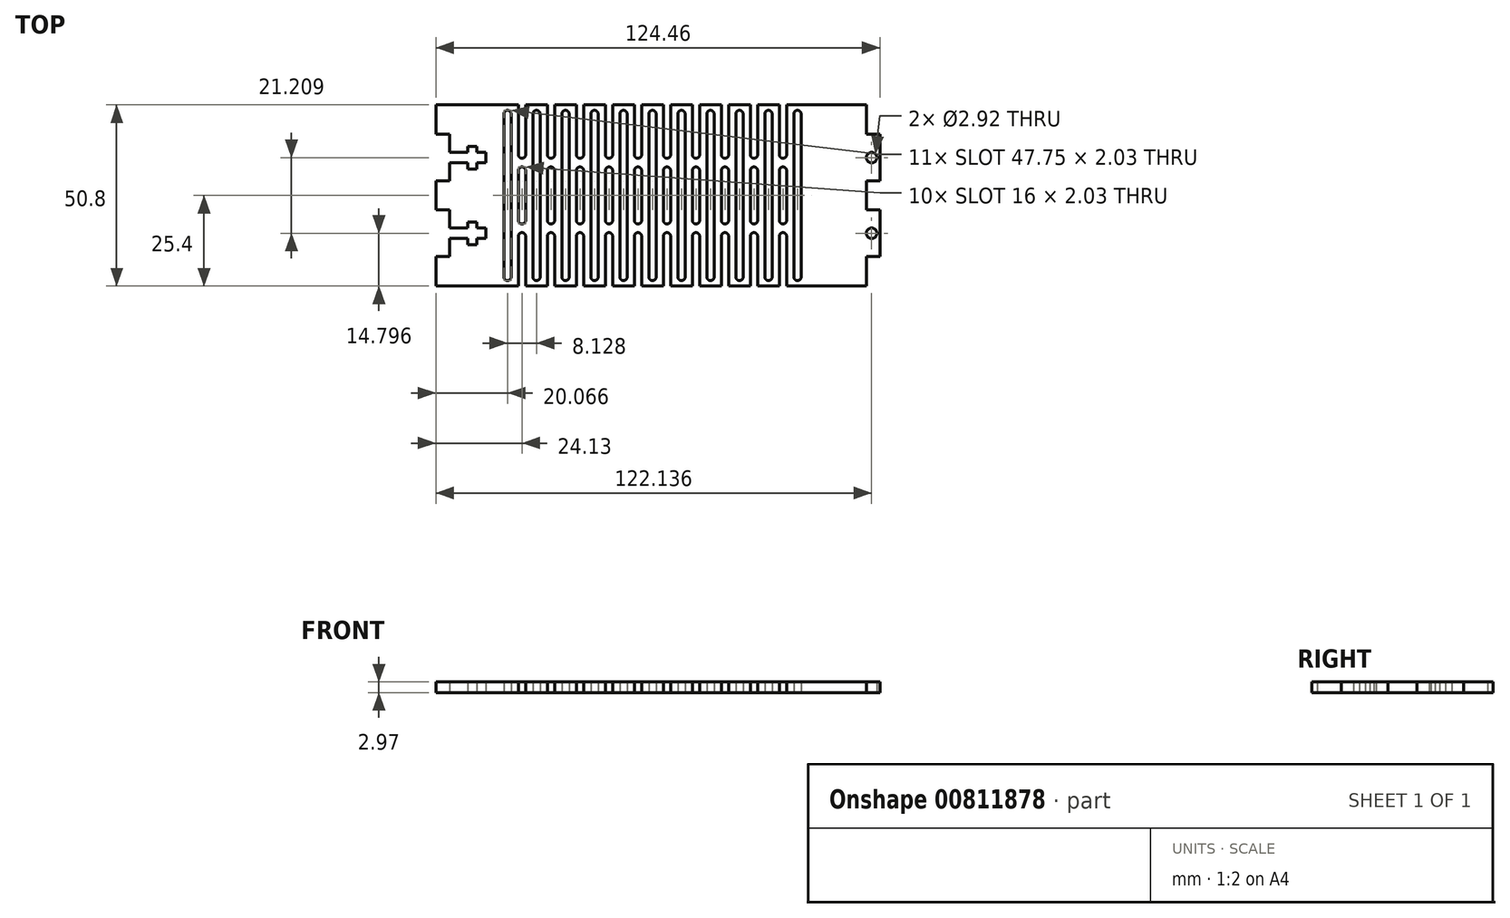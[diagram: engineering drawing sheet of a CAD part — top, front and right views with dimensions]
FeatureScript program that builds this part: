
annotation { "Feature Type Name" : "Feature", "Feature Type Description" : "" }
export const myFeature = defineFeature(function(context is Context, id is Id, definition is map)
    precondition{}
    {
        {
            var Q0;
            Q0=qCreatedBy(makeId("Top.planeOp"),FACE);
            var sketch = newSketch(context, id + "F0", { "sketchPlane" : qUnion([Q0])});
            skLineSegment(sketch, "E0", {"start": v(0, 8.26) * mm, "end": v(3.81, 8.26) * mm});
            skLineSegment(sketch, "E1", {"start": v(3.81, 8.26) * mm, "end": v(3.81, 13.34) * mm});
            skLineSegment(sketch, "E2", {"start": v(3.81, 13.34) * mm, "end": v(8.9, 13.34) * mm});
            skLineSegment(sketch, "E3", {"start": v(8.9, 13.34) * mm, "end": v(8.9, 11.6) * mm});
            skLineSegment(sketch, "E4", {"start": v(8.9, 11.6) * mm, "end": v(11.43, 11.6) * mm});
            skLineSegment(sketch, "E5", {"start": v(11.43, 11.6) * mm, "end": v(11.43, 13.34) * mm});
            skLineSegment(sketch, "E6", {"start": v(11.43, 13.34) * mm, "end": v(13.97, 13.34) * mm});
            skLineSegment(sketch, "E7", {"start": v(13.97, 13.34) * mm, "end": v(13.97, 16.26) * mm});
            skLineSegment(sketch, "E8", {"start": v(13.97, 16.26) * mm, "end": v(11.43, 16.26) * mm});
            skLineSegment(sketch, "E9", {"start": v(11.43, 16.26) * mm, "end": v(11.43, 17.98) * mm});
            skLineSegment(sketch, "E10", {"start": v(11.43, 17.98) * mm, "end": v(8.9, 17.98) * mm});
            skLineSegment(sketch, "E11", {"start": v(8.9, 17.98) * mm, "end": v(8.9, 16.26) * mm});
            skLineSegment(sketch, "E12", {"start": v(8.9, 16.26) * mm, "end": v(3.81, 16.26) * mm});
            skLineSegment(sketch, "E13", {"start": v(3.81, 16.26) * mm, "end": v(3.81, 21.34) * mm});
            skLineSegment(sketch, "E14", {"start": v(3.81, 21.34) * mm, "end": v(0, 21.34) * mm});
            skLineSegment(sketch, "E15", {"start": v(0, 0) * mm, "end": v(0, 8.26) * mm});
            skLineSegment(sketch, "E16", {"start": v(0, 50.8) * mm, "end": v(0, 42.55) * mm});
            skLineSegment(sketch, "E17", {"start": v(0, 42.55) * mm, "end": v(3.81, 42.55) * mm});
            skLineSegment(sketch, "E18", {"start": v(3.81, 42.54) * mm, "end": v(3.81, 37.46) * mm});
            skLineSegment(sketch, "E19", {"start": v(3.81, 37.46) * mm, "end": v(8.89, 37.46) * mm});
            skLineSegment(sketch, "E20", {"start": v(8.89, 37.46) * mm, "end": v(8.89, 39.2) * mm});
            skLineSegment(sketch, "E21", {"start": v(8.89, 39.2) * mm, "end": v(11.43, 39.2) * mm});
            skLineSegment(sketch, "E22", {"start": v(11.43, 39.2) * mm, "end": v(11.43, 37.46) * mm});
            skLineSegment(sketch, "E23", {"start": v(11.43, 37.46) * mm, "end": v(13.97, 37.46) * mm});
            skLineSegment(sketch, "E24", {"start": v(13.97, 37.46) * mm, "end": v(13.97, 34.54) * mm});
            skLineSegment(sketch, "E25", {"start": v(13.97, 34.54) * mm, "end": v(11.43, 34.54) * mm});
            skLineSegment(sketch, "E26", {"start": v(11.43, 34.54) * mm, "end": v(11.43, 32.82) * mm});
            skLineSegment(sketch, "E27", {"start": v(11.43, 32.82) * mm, "end": v(8.89, 32.82) * mm});
            skLineSegment(sketch, "E28", {"start": v(8.89, 32.82) * mm, "end": v(8.89, 34.54) * mm});
            skLineSegment(sketch, "E29", {"start": v(8.89, 34.54) * mm, "end": v(3.81, 34.54) * mm});
            skLineSegment(sketch, "E30", {"start": v(3.81, 34.54) * mm, "end": v(3.81, 29.46) * mm});
            skLineSegment(sketch, "E31", {"start": v(3.81, 29.46) * mm, "end": v(0, 29.46) * mm});
            skLineSegment(sketch, "E32", {"start": v(0, 29.46) * mm, "end": v(0, 21.34) * mm});
            skLineSegment(sketch, "E33", {"start": v(120.65, 0) * mm, "end": v(120.65, 8.26) * mm});
            skLineSegment(sketch, "E34", {"start": v(120.65, 8.26) * mm, "end": v(124.46, 8.26) * mm});
            skLineSegment(sketch, "E35", {"start": v(124.46, 8.26) * mm, "end": v(124.46, 21.34) * mm});
            skLineSegment(sketch, "E36", {"start": v(124.46, 21.34) * mm, "end": v(120.65, 21.34) * mm});
            skLineSegment(sketch, "E37", {"start": v(120.65, 21.34) * mm, "end": v(120.65, 29.46) * mm});
            skLineSegment(sketch, "E38", {"start": v(120.65, 29.46) * mm, "end": v(124.46, 29.46) * mm});
            skLineSegment(sketch, "E39", {"start": v(124.46, 29.46) * mm, "end": v(124.46, 42.55) * mm});
            skLineSegment(sketch, "E40", {"start": v(124.46, 42.55) * mm, "end": v(120.65, 42.55) * mm});
            skLineSegment(sketch, "E41", {"start": v(120.65, 42.55) * mm, "end": v(120.65, 50.8) * mm});
            skCircle(sketch, "E42", {"center": v(122.14, 14.8) * mm, "radius": 1.46 * mm});
            skCircle(sketch, "E43", {"center": v(122.14, 36) * mm, "radius": 1.46 * mm});
            skLineSegment(sketch, "E44", {"start": v(19.05, 2.54) * mm, "end": v(19.05, 48.26) * mm});
            skLineSegment(sketch, "E45", {"start": v(21.08, 2.54) * mm, "end": v(21.08, 48.26) * mm});
            skArc(sketch, "E46", {"start": v(19.05, 48.26) * mm, "mid": v(20.07, 49.28) * mm, "end": v(21.08, 48.26) * mm});
            skArc(sketch, "E47", {"start": v(19.05, 2.54) * mm, "mid": v(20.07, 1.52) * mm, "end": v(21.08, 2.54) * mm});
            skLineSegment(sketch, "E48", {"start": v(23.11, 50.8) * mm, "end": v(23.11, 36.83) * mm});
            skLineSegment(sketch, "E49", {"start": v(0, 50.8) * mm, "end": v(23.11, 50.8) * mm});
            skLineSegment(sketch, "E50", {"start": v(0, 0) * mm, "end": v(23.11, 0) * mm});
            skLineSegment(sketch, "E51", {"start": v(25.15, 50.8) * mm, "end": v(25.15, 36.83) * mm});
            skArc(sketch, "E52", {"start": v(23.11, 36.83) * mm, "mid": v(24.13, 35.81) * mm, "end": v(25.15, 36.83) * mm});
            skLineSegment(sketch, "E53", {"start": v(23.11, 32.39) * mm, "end": v(23.11, 18.42) * mm});
            skLineSegment(sketch, "E54", {"start": v(25.15, 32.39) * mm, "end": v(25.15, 18.42) * mm});
            skLineSegment(sketch, "E55", {"start": v(23.11, 0) * mm, "end": v(23.11, 13.97) * mm});
            skLineSegment(sketch, "E56", {"start": v(25.15, 13.97) * mm, "end": v(25.15, 0) * mm});
            skArc(sketch, "E57", {"start": v(23.11, 32.39) * mm, "mid": v(24.13, 33.4) * mm, "end": v(25.15, 32.39) * mm});
            skArc(sketch, "E58", {"start": v(23.11, 18.42) * mm, "mid": v(24.13, 17.4) * mm, "end": v(25.15, 18.42) * mm});
            skArc(sketch, "E59", {"start": v(25.15, 13.97) * mm, "mid": v(24.13, 14.99) * mm, "end": v(23.11, 13.97) * mm});
            skLineSegment(sketch, "E60", {"start": v(25.15, 50.8) * mm, "end": v(31.24, 50.8) * mm});
            skLineSegment(sketch, "E61", {"start": v(25.15, 0) * mm, "end": v(31.24, 0) * mm});
            skLineSegment(sketch, "E62", {"start": v(27.18, 2.54) * mm, "end": v(27.18, 48.26) * mm});
            skLineSegment(sketch, "E63", {"start": v(29.2, 2.54) * mm, "end": v(29.2, 48.26) * mm});
            skArc(sketch, "E64", {"start": v(27.18, 48.26) * mm, "mid": v(28.2, 49.28) * mm, "end": v(29.2, 48.26) * mm});
            skArc(sketch, "E65", {"start": v(27.18, 2.54) * mm, "mid": v(28.2, 1.52) * mm, "end": v(29.2, 2.54) * mm});
            skLineSegment(sketch, "E66", {"start": v(31.24, 50.8) * mm, "end": v(31.24, 36.83) * mm});
            skLineSegment(sketch, "E67", {"start": v(33.27, 50.8) * mm, "end": v(33.27, 36.83) * mm});
            skArc(sketch, "E68", {"start": v(31.24, 36.83) * mm, "mid": v(32.26, 35.81) * mm, "end": v(33.27, 36.83) * mm});
            skLineSegment(sketch, "E69", {"start": v(31.24, 32.39) * mm, "end": v(31.24, 18.42) * mm});
            skLineSegment(sketch, "E70", {"start": v(33.27, 32.39) * mm, "end": v(33.27, 18.42) * mm});
            skLineSegment(sketch, "E71", {"start": v(31.24, 0) * mm, "end": v(31.24, 13.97) * mm});
            skLineSegment(sketch, "E72", {"start": v(33.27, 13.97) * mm, "end": v(33.27, 0) * mm});
            skArc(sketch, "E73", {"start": v(31.24, 32.39) * mm, "mid": v(32.26, 33.4) * mm, "end": v(33.27, 32.39) * mm});
            skArc(sketch, "E74", {"start": v(31.24, 18.42) * mm, "mid": v(32.26, 17.4) * mm, "end": v(33.27, 18.42) * mm});
            skArc(sketch, "E75", {"start": v(33.27, 13.97) * mm, "mid": v(32.26, 14.99) * mm, "end": v(31.24, 13.97) * mm});
            skLineSegment(sketch, "E76", {"start": v(33.27, 0) * mm, "end": v(39.37, 0) * mm});
            skLineSegment(sketch, "E77", {"start": v(35.3, 2.54) * mm, "end": v(35.3, 48.26) * mm});
            skLineSegment(sketch, "E78", {"start": v(37.34, 2.54) * mm, "end": v(37.34, 48.26) * mm});
            skArc(sketch, "E79", {"start": v(35.3, 48.26) * mm, "mid": v(36.32, 49.28) * mm, "end": v(37.34, 48.26) * mm});
            skArc(sketch, "E80", {"start": v(35.3, 2.54) * mm, "mid": v(36.32, 1.52) * mm, "end": v(37.34, 2.54) * mm});
            skLineSegment(sketch, "E81", {"start": v(39.37, 50.8) * mm, "end": v(39.37, 36.83) * mm});
            skLineSegment(sketch, "E82", {"start": v(41.4, 50.8) * mm, "end": v(41.4, 36.83) * mm});
            skArc(sketch, "E83", {"start": v(39.37, 36.83) * mm, "mid": v(40.39, 35.81) * mm, "end": v(41.4, 36.83) * mm});
            skLineSegment(sketch, "E84", {"start": v(39.37, 32.39) * mm, "end": v(39.37, 18.42) * mm});
            skLineSegment(sketch, "E85", {"start": v(41.4, 32.39) * mm, "end": v(41.4, 18.42) * mm});
            skLineSegment(sketch, "E86", {"start": v(39.37, 0) * mm, "end": v(39.37, 13.97) * mm});
            skLineSegment(sketch, "E87", {"start": v(41.4, 13.97) * mm, "end": v(41.4, 0) * mm});
            skArc(sketch, "E88", {"start": v(39.37, 32.39) * mm, "mid": v(40.39, 33.4) * mm, "end": v(41.4, 32.39) * mm});
            skArc(sketch, "E89", {"start": v(39.37, 18.42) * mm, "mid": v(40.39, 17.4) * mm, "end": v(41.4, 18.42) * mm});
            skArc(sketch, "E90", {"start": v(41.4, 13.97) * mm, "mid": v(40.39, 14.99) * mm, "end": v(39.37, 13.97) * mm});
            skLineSegment(sketch, "E91", {"start": v(41.4, 50.8) * mm, "end": v(47.5, 50.8) * mm});
            skLineSegment(sketch, "E92", {"start": v(43.43, 2.54) * mm, "end": v(43.43, 48.26) * mm});
            skLineSegment(sketch, "E93", {"start": v(45.47, 2.54) * mm, "end": v(45.47, 48.26) * mm});
            skArc(sketch, "E94", {"start": v(43.43, 48.26) * mm, "mid": v(44.45, 49.28) * mm, "end": v(45.47, 48.26) * mm});
            skArc(sketch, "E95", {"start": v(43.43, 2.54) * mm, "mid": v(44.45, 1.52) * mm, "end": v(45.47, 2.54) * mm});
            skLineSegment(sketch, "E96", {"start": v(47.5, 50.8) * mm, "end": v(47.5, 36.83) * mm});
            skLineSegment(sketch, "E97", {"start": v(49.53, 50.8) * mm, "end": v(49.53, 36.83) * mm});
            skArc(sketch, "E98", {"start": v(47.5, 36.83) * mm, "mid": v(48.51, 35.81) * mm, "end": v(49.53, 36.83) * mm});
            skLineSegment(sketch, "E99", {"start": v(47.5, 32.39) * mm, "end": v(47.5, 18.42) * mm});
            skLineSegment(sketch, "E100", {"start": v(49.53, 32.39) * mm, "end": v(49.53, 18.42) * mm});
            skLineSegment(sketch, "E101", {"start": v(47.5, 0) * mm, "end": v(47.5, 13.97) * mm});
            skLineSegment(sketch, "E102", {"start": v(49.53, 13.97) * mm, "end": v(49.53, 0) * mm});
            skArc(sketch, "E103", {"start": v(47.5, 32.39) * mm, "mid": v(48.51, 33.4) * mm, "end": v(49.53, 32.39) * mm});
            skArc(sketch, "E104", {"start": v(47.5, 18.42) * mm, "mid": v(48.51, 17.4) * mm, "end": v(49.53, 18.42) * mm});
            skArc(sketch, "E105", {"start": v(49.53, 13.97) * mm, "mid": v(48.51, 14.99) * mm, "end": v(47.5, 13.97) * mm});
            skLineSegment(sketch, "E106", {"start": v(49.53, 50.8) * mm, "end": v(55.63, 50.8) * mm});
            skLineSegment(sketch, "E107", {"start": v(49.53, 0) * mm, "end": v(55.63, 0) * mm});
            skLineSegment(sketch, "E108", {"start": v(33.27, 50.8) * mm, "end": v(39.37, 50.8) * mm});
            skLineSegment(sketch, "E109", {"start": v(41.4, 0) * mm, "end": v(47.5, 0) * mm});
            skLineSegment(sketch, "E110", {"start": v(51.56, 2.54) * mm, "end": v(51.56, 48.26) * mm});
            skLineSegment(sketch, "E111", {"start": v(53.6, 2.54) * mm, "end": v(53.6, 48.26) * mm});
            skArc(sketch, "E112", {"start": v(51.56, 48.26) * mm, "mid": v(52.58, 49.28) * mm, "end": v(53.6, 48.26) * mm});
            skArc(sketch, "E113", {"start": v(51.56, 2.54) * mm, "mid": v(52.58, 1.52) * mm, "end": v(53.6, 2.54) * mm});
            skLineSegment(sketch, "E114", {"start": v(55.63, 50.8) * mm, "end": v(55.63, 36.83) * mm});
            skLineSegment(sketch, "E115", {"start": v(57.66, 50.8) * mm, "end": v(57.66, 36.83) * mm});
            skArc(sketch, "E116", {"start": v(55.63, 36.83) * mm, "mid": v(56.64, 35.81) * mm, "end": v(57.66, 36.83) * mm});
            skLineSegment(sketch, "E117", {"start": v(55.63, 32.39) * mm, "end": v(55.63, 18.42) * mm});
            skLineSegment(sketch, "E118", {"start": v(57.66, 32.39) * mm, "end": v(57.66, 18.42) * mm});
            skLineSegment(sketch, "E119", {"start": v(55.63, 0) * mm, "end": v(55.63, 13.97) * mm});
            skLineSegment(sketch, "E120", {"start": v(57.66, 13.97) * mm, "end": v(57.66, 0) * mm});
            skArc(sketch, "E121", {"start": v(55.63, 32.39) * mm, "mid": v(56.64, 33.4) * mm, "end": v(57.66, 32.39) * mm});
            skArc(sketch, "E122", {"start": v(55.63, 18.42) * mm, "mid": v(56.64, 17.4) * mm, "end": v(57.66, 18.42) * mm});
            skArc(sketch, "E123", {"start": v(57.66, 13.97) * mm, "mid": v(56.64, 14.99) * mm, "end": v(55.63, 13.97) * mm});
            skLineSegment(sketch, "E124", {"start": v(57.66, 50.8) * mm, "end": v(63.75, 50.8) * mm});
            skLineSegment(sketch, "E125", {"start": v(57.66, 0) * mm, "end": v(63.75, 0) * mm});
            skLineSegment(sketch, "E126", {"start": v(59.7, 2.54) * mm, "end": v(59.7, 48.26) * mm});
            skLineSegment(sketch, "E127", {"start": v(61.72, 2.54) * mm, "end": v(61.72, 48.26) * mm});
            skArc(sketch, "E128", {"start": v(59.69, 48.26) * mm, "mid": v(60.7, 49.28) * mm, "end": v(61.72, 48.26) * mm});
            skArc(sketch, "E129", {"start": v(59.69, 2.54) * mm, "mid": v(60.7, 1.52) * mm, "end": v(61.72, 2.54) * mm});
            skLineSegment(sketch, "E130", {"start": v(63.75, 50.8) * mm, "end": v(63.75, 36.83) * mm});
            skLineSegment(sketch, "E131", {"start": v(65.79, 50.8) * mm, "end": v(65.79, 36.83) * mm});
            skArc(sketch, "E132", {"start": v(63.75, 36.83) * mm, "mid": v(64.77, 35.81) * mm, "end": v(65.79, 36.83) * mm});
            skLineSegment(sketch, "E133", {"start": v(63.75, 32.39) * mm, "end": v(63.75, 18.42) * mm});
            skLineSegment(sketch, "E134", {"start": v(65.79, 32.39) * mm, "end": v(65.79, 18.42) * mm});
            skLineSegment(sketch, "E135", {"start": v(63.75, 0) * mm, "end": v(63.75, 13.97) * mm});
            skLineSegment(sketch, "E136", {"start": v(65.79, 13.97) * mm, "end": v(65.79, 0) * mm});
            skArc(sketch, "E137", {"start": v(63.75, 32.39) * mm, "mid": v(64.77, 33.4) * mm, "end": v(65.79, 32.39) * mm});
            skArc(sketch, "E138", {"start": v(63.75, 18.42) * mm, "mid": v(64.77, 17.4) * mm, "end": v(65.79, 18.42) * mm});
            skArc(sketch, "E139", {"start": v(65.79, 13.97) * mm, "mid": v(64.77, 14.99) * mm, "end": v(63.75, 13.97) * mm});
            skLineSegment(sketch, "E140", {"start": v(65.79, 0) * mm, "end": v(71.88, 0) * mm});
            skLineSegment(sketch, "E141", {"start": v(67.82, 2.54) * mm, "end": v(67.82, 48.26) * mm});
            skLineSegment(sketch, "E142", {"start": v(69.85, 2.54) * mm, "end": v(69.85, 48.26) * mm});
            skArc(sketch, "E143", {"start": v(67.82, 48.26) * mm, "mid": v(68.83, 49.28) * mm, "end": v(69.85, 48.26) * mm});
            skArc(sketch, "E144", {"start": v(67.82, 2.54) * mm, "mid": v(68.83, 1.52) * mm, "end": v(69.85, 2.54) * mm});
            skLineSegment(sketch, "E145", {"start": v(71.88, 50.8) * mm, "end": v(71.88, 36.83) * mm});
            skLineSegment(sketch, "E146", {"start": v(73.91, 50.8) * mm, "end": v(73.91, 36.83) * mm});
            skArc(sketch, "E147", {"start": v(71.88, 36.83) * mm, "mid": v(72.9, 35.81) * mm, "end": v(73.91, 36.83) * mm});
            skLineSegment(sketch, "E148", {"start": v(71.88, 32.39) * mm, "end": v(71.88, 18.42) * mm});
            skLineSegment(sketch, "E149", {"start": v(73.91, 32.39) * mm, "end": v(73.91, 18.42) * mm});
            skLineSegment(sketch, "E150", {"start": v(71.88, 0) * mm, "end": v(71.88, 13.97) * mm});
            skLineSegment(sketch, "E151", {"start": v(73.91, 13.97) * mm, "end": v(73.91, 0) * mm});
            skArc(sketch, "E152", {"start": v(71.88, 32.39) * mm, "mid": v(72.9, 33.4) * mm, "end": v(73.91, 32.39) * mm});
            skArc(sketch, "E153", {"start": v(71.88, 18.42) * mm, "mid": v(72.9, 17.4) * mm, "end": v(73.91, 18.42) * mm});
            skArc(sketch, "E154", {"start": v(73.91, 13.97) * mm, "mid": v(72.9, 14.99) * mm, "end": v(71.88, 13.97) * mm});
            skLineSegment(sketch, "E155", {"start": v(73.91, 50.8) * mm, "end": v(80.01, 50.8) * mm});
            skLineSegment(sketch, "E156", {"start": v(75.95, 2.54) * mm, "end": v(75.95, 48.26) * mm});
            skLineSegment(sketch, "E157", {"start": v(77.98, 2.54) * mm, "end": v(77.98, 48.26) * mm});
            skArc(sketch, "E158", {"start": v(75.95, 48.26) * mm, "mid": v(76.96, 49.28) * mm, "end": v(77.98, 48.26) * mm});
            skArc(sketch, "E159", {"start": v(75.95, 2.54) * mm, "mid": v(76.96, 1.52) * mm, "end": v(77.98, 2.54) * mm});
            skLineSegment(sketch, "E160", {"start": v(80.01, 50.8) * mm, "end": v(80.01, 36.83) * mm});
            skLineSegment(sketch, "E161", {"start": v(82.04, 50.8) * mm, "end": v(82.04, 36.83) * mm});
            skArc(sketch, "E162", {"start": v(80.01, 36.83) * mm, "mid": v(81.03, 35.81) * mm, "end": v(82.04, 36.83) * mm});
            skLineSegment(sketch, "E163", {"start": v(80.01, 32.39) * mm, "end": v(80.01, 18.42) * mm});
            skLineSegment(sketch, "E164", {"start": v(82.04, 32.39) * mm, "end": v(82.04, 18.42) * mm});
            skLineSegment(sketch, "E165", {"start": v(80.01, 0) * mm, "end": v(80.01, 13.97) * mm});
            skLineSegment(sketch, "E166", {"start": v(82.04, 13.97) * mm, "end": v(82.04, 0) * mm});
            skArc(sketch, "E167", {"start": v(80.01, 32.39) * mm, "mid": v(81.03, 33.4) * mm, "end": v(82.04, 32.39) * mm});
            skArc(sketch, "E168", {"start": v(80.01, 18.42) * mm, "mid": v(81.03, 17.4) * mm, "end": v(82.04, 18.42) * mm});
            skArc(sketch, "E169", {"start": v(82.04, 13.97) * mm, "mid": v(81.03, 14.99) * mm, "end": v(80.01, 13.97) * mm});
            skLineSegment(sketch, "E170", {"start": v(65.79, 50.8) * mm, "end": v(71.88, 50.8) * mm});
            skLineSegment(sketch, "E171", {"start": v(73.91, 0) * mm, "end": v(80.01, 0) * mm});
            skLineSegment(sketch, "E172", {"start": v(84.07, 2.54) * mm, "end": v(84.07, 48.26) * mm});
            skLineSegment(sketch, "E173", {"start": v(86.1, 2.54) * mm, "end": v(86.1, 48.26) * mm});
            skArc(sketch, "E174", {"start": v(84.07, 48.26) * mm, "mid": v(85.09, 49.28) * mm, "end": v(86.1, 48.26) * mm});
            skArc(sketch, "E175", {"start": v(84.07, 2.54) * mm, "mid": v(85.09, 1.52) * mm, "end": v(86.1, 2.54) * mm});
            skLineSegment(sketch, "E176", {"start": v(88.14, 50.8) * mm, "end": v(88.14, 36.83) * mm});
            skLineSegment(sketch, "E177", {"start": v(90.17, 50.8) * mm, "end": v(90.17, 36.83) * mm});
            skArc(sketch, "E178", {"start": v(88.14, 36.83) * mm, "mid": v(89.15, 35.81) * mm, "end": v(90.17, 36.83) * mm});
            skLineSegment(sketch, "E179", {"start": v(88.14, 32.39) * mm, "end": v(88.14, 18.42) * mm});
            skLineSegment(sketch, "E180", {"start": v(90.17, 32.39) * mm, "end": v(90.17, 18.42) * mm});
            skLineSegment(sketch, "E181", {"start": v(88.14, 0) * mm, "end": v(88.14, 13.97) * mm});
            skLineSegment(sketch, "E182", {"start": v(90.17, 13.97) * mm, "end": v(90.17, 0) * mm});
            skArc(sketch, "E183", {"start": v(88.14, 32.39) * mm, "mid": v(89.15, 33.4) * mm, "end": v(90.17, 32.39) * mm});
            skArc(sketch, "E184", {"start": v(88.14, 18.42) * mm, "mid": v(89.15, 17.4) * mm, "end": v(90.17, 18.42) * mm});
            skArc(sketch, "E185", {"start": v(90.17, 13.97) * mm, "mid": v(89.15, 14.99) * mm, "end": v(88.14, 13.97) * mm});
            skLineSegment(sketch, "E186", {"start": v(82.04, 0) * mm, "end": v(88.14, 0) * mm});
            skLineSegment(sketch, "E187", {"start": v(82.04, 50.8) * mm, "end": v(88.14, 50.8) * mm});
            skLineSegment(sketch, "E188", {"start": v(92.2, 2.54) * mm, "end": v(92.2, 48.26) * mm});
            skLineSegment(sketch, "E189", {"start": v(94.23, 2.54) * mm, "end": v(94.23, 48.26) * mm});
            skArc(sketch, "E190", {"start": v(92.2, 48.26) * mm, "mid": v(93.22, 49.28) * mm, "end": v(94.23, 48.26) * mm});
            skArc(sketch, "E191", {"start": v(92.2, 2.54) * mm, "mid": v(93.22, 1.52) * mm, "end": v(94.23, 2.54) * mm});
            skLineSegment(sketch, "E192", {"start": v(120.65, 50.8) * mm, "end": v(98.3, 50.8) * mm});
            skLineSegment(sketch, "E193", {"start": v(120.65, 0) * mm, "end": v(98.3, 0) * mm});
            skLineSegment(sketch, "E194", {"start": v(96.27, 50.8) * mm, "end": v(96.27, 36.83) * mm});
            skLineSegment(sketch, "E195", {"start": v(98.3, 50.8) * mm, "end": v(98.3, 36.83) * mm});
            skArc(sketch, "E196", {"start": v(96.27, 36.83) * mm, "mid": v(97.28, 35.81) * mm, "end": v(98.3, 36.83) * mm});
            skLineSegment(sketch, "E197", {"start": v(96.27, 32.39) * mm, "end": v(96.27, 18.42) * mm});
            skLineSegment(sketch, "E198", {"start": v(98.3, 32.39) * mm, "end": v(98.3, 18.42) * mm});
            skLineSegment(sketch, "E199", {"start": v(96.27, 0) * mm, "end": v(96.27, 13.97) * mm});
            skLineSegment(sketch, "E200", {"start": v(98.3, 13.97) * mm, "end": v(98.3, 0) * mm});
            skArc(sketch, "E201", {"start": v(96.27, 32.39) * mm, "mid": v(97.28, 33.4) * mm, "end": v(98.3, 32.39) * mm});
            skArc(sketch, "E202", {"start": v(96.27, 18.42) * mm, "mid": v(97.28, 17.4) * mm, "end": v(98.3, 18.42) * mm});
            skArc(sketch, "E203", {"start": v(98.3, 13.97) * mm, "mid": v(97.28, 14.99) * mm, "end": v(96.27, 13.97) * mm});
            skLineSegment(sketch, "E204", {"start": v(100.33, 2.54) * mm, "end": v(100.33, 48.26) * mm});
            skLineSegment(sketch, "E205", {"start": v(102.36, 2.54) * mm, "end": v(102.36, 48.26) * mm});
            skArc(sketch, "E206", {"start": v(100.33, 48.26) * mm, "mid": v(101.35, 49.28) * mm, "end": v(102.36, 48.26) * mm});
            skArc(sketch, "E207", {"start": v(100.33, 2.54) * mm, "mid": v(101.35, 1.52) * mm, "end": v(102.36, 2.54) * mm});
            skLineSegment(sketch, "E208", {"start": v(90.17, 0) * mm, "end": v(96.27, 0) * mm});
            skLineSegment(sketch, "E209", {"start": v(90.17, 50.8) * mm, "end": v(96.27, 50.8) * mm});
            skSolve(sketch);
        }
        {
            var Q0;
            Q0=makeQuery(id+"F0.imprint","IMPRINT",FACE,{"disambiguationData":[TD([[makeQuery(id+"F0.imprint","IMPRINT",EDGE,{"derivedFrom":sQuery(id+"F0.wireOp",EDGE,"E0")}),-1.0]])]});
            extrude(context, id + "F1", {"entities" : qUnion([Q0]), "depth" : 2.97 * mm, "offsetDistance" : 25.4 * mm});
        }
    });
